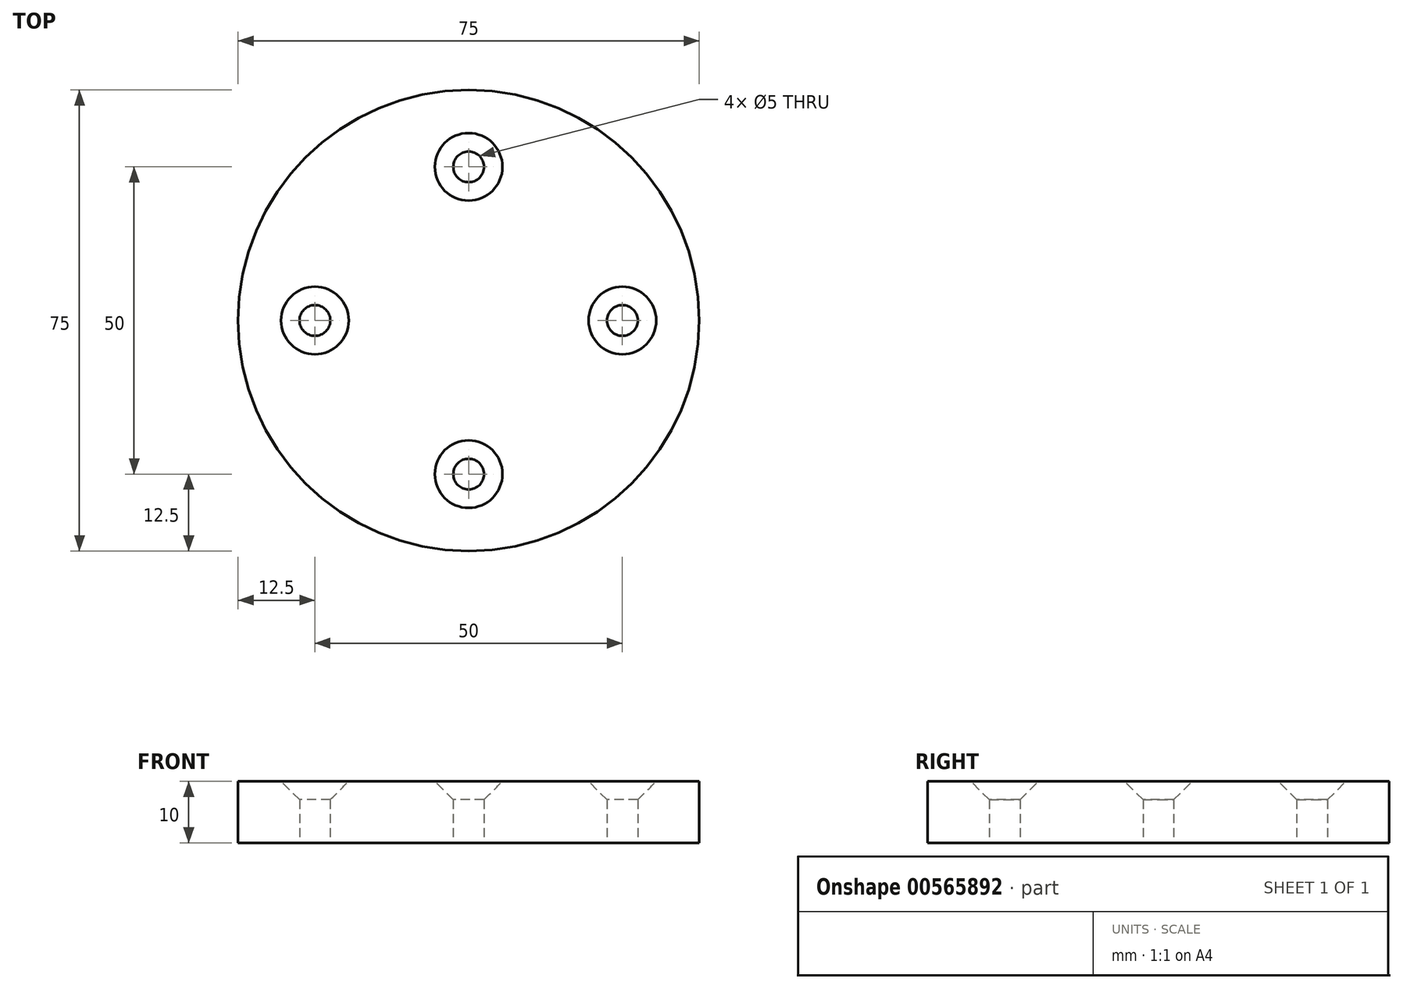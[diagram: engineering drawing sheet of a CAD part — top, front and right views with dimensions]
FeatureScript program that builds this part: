
annotation { "Feature Type Name" : "Feature", "Feature Type Description" : "" }
export const myFeature = defineFeature(function(context is Context, id is Id, definition is map)
    precondition{}
    {
        {
            var Q0;
            Q0=qCreatedBy(makeId("Top.planeOp"),FACE);
            var sketch = newSketch(context, id + "F0", { "sketchPlane" : qUnion([Q0])});
            skCircle(sketch, "E0", {"center": v(0, 0) * mm, "radius": 37.5 * mm});
            skCircle(sketch, "E1", {"center": v(0, 25) * mm, "radius": 2.5 * mm});
            skCircle(sketch, "E2.1.0", {"center": v(-25, 0) * mm, "radius": 2.5 * mm});
            skCircle(sketch, "E2.2.0", {"center": v(0, -25) * mm, "radius": 2.5 * mm});
            skCircle(sketch, "E2.3.0", {"center": v(25, 0) * mm, "radius": 2.5 * mm});
            skSolve(sketch);
        }
        {
            var Q0;
            Q0=makeQuery(id+"F0.imprint","IMPRINT",FACE,{"disambiguationData":[TD([[makeQuery(id+"F0.imprint","IMPRINT",EDGE,{"derivedFrom":sQuery(id+"F0.wireOp",EDGE,"E0")}),1.0]])]});
            extrude(context, id + "F1", {"entities" : qUnion([Q0]), "depth" : 10 * mm, "offsetDistance" : 25 * mm});
        }
        {
            var Q0;
            Q0=makeQuery(id+"F1.opExtrude","CAP_EDGE",EDGE,{"disambiguationData":[OSD([sQuery(id+"F0.wireOp",EDGE,"E1")])],"isStart":false});
            var Q1;
            Q1=makeQuery(id+"F1.opExtrude","CAP_EDGE",EDGE,{"disambiguationData":[OSD([sQuery(id+"F0.wireOp",EDGE,"E2.3.0")])],"isStart":false});
            var Q2;
            Q2=makeQuery(id+"F1.opExtrude","CAP_EDGE",EDGE,{"disambiguationData":[OSD([sQuery(id+"F0.wireOp",EDGE,"E2.2.0")])],"isStart":false});
            var Q3;
            Q3=makeQuery(id+"F1.opExtrude","CAP_EDGE",EDGE,{"disambiguationData":[OSD([sQuery(id+"F0.wireOp",EDGE,"E2.1.0")])],"isStart":false});
            chamfer(context, id + "F2", {"entities" : qUnion([Q0, Q1, Q2, Q3]), "width" : 3 * mm, "tangentPropagation" : true});
        }
    });
